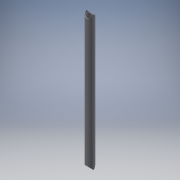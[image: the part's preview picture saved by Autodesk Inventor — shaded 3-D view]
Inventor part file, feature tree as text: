
AUTODESK INVENTOR PART (.ipt)
format: ipt  version: 2018 (Build 220112000, 112)  size: 115,200 bytes
history: native  units: mm
features: sketch x4, extrude x3, other x2, hole x1
ambient origin geometry x8: Origin, YZ Plane, XZ Plane, XY Plane, X Axis, Y Axis, Z Axis, Center Point
bodies: Body1 (feature_tree)
feature tree (10):
  other  "ソリッド1"
  extrude  "押し出し1"  Depth=27.2mm
  hole  "穴1"  [1 undecoded]
  other  "作業平面1"
  extrude  "押し出し3"  TaperAngle=0.0deg  [1 undecoded]
  extrude  "押し出し4"  Depth=27.2mm TaperAngle=0.0deg
  sketch  "スケッチ1"
  sketch  "スケッチ3"
  sketch  "スケッチ4"
  sketch  "スケッチ5"
note: 2 required parameter values undecoded (feature->parameter linkage not recoverable at this tier; creation-order binding heuristic only, values carry confidence <= 0.55)
